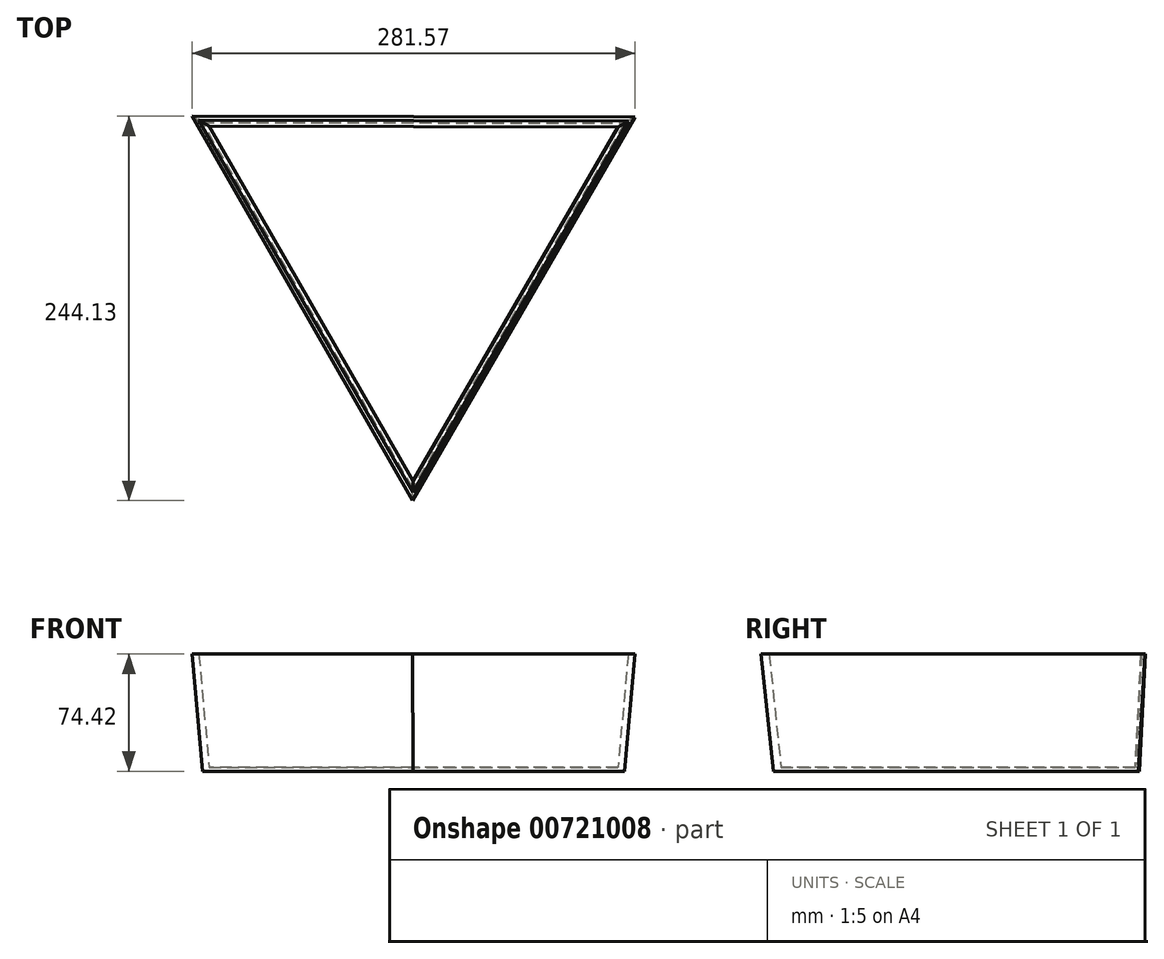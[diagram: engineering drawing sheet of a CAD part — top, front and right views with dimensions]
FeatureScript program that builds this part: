
annotation { "Feature Type Name" : "Feature", "Feature Type Description" : "" }
export const myFeature = defineFeature(function(context is Context, id is Id, definition is map)
    precondition{}
    {
        {
            var Q0;
            Q0=qCreatedBy(makeId("Top.planeOp"),FACE);
            var sketch = newSketch(context, id + "F0", { "sketchPlane" : qUnion([Q0])});
            skCircle(sketch, "E0.cCircle", {"center": v(0, -27.9) * mm, "radius": 77.38 * mm, "construction": true});
            skLineSegment(sketch, "E0.0", {"start": v(134.19, 49.2) * mm, "end": v(-0.32, -182.67) * mm});
            skLineSegment(sketch, "E0.1", {"start": v(-0.32, -182.67) * mm, "end": v(-133.87, 49.75) * mm});
            skLineSegment(sketch, "E0.2", {"start": v(-133.87, 49.75) * mm, "end": v(134.19, 49.2) * mm});
            skPoint(sketch, "E0.0.midPoint", {"position": v(66.94, -66.74) * mm});
            skSolve(sketch);
        }
        {
            var Q0;
            Q0=makeQuery(id+"F0.imprint","IMPRINT",FACE,{"disambiguationData":[TD([[makeQuery(id+"F0.imprint","IMPRINT",EDGE,{"derivedFrom":sQuery(id+"F0.wireOp",EDGE,"E0.0")}),-1.0]])]});
            extrude(context, id + "F1", {"entities" : qUnion([Q0]), "depth" : 74.42 * mm, "offsetDistance" : 25.4 * mm, "hasDraft" : true, "draftAngle" : 3 * degree});
        }
        {
            var Q0;
            Q0=makeQuery(id+"F1.opExtrude","CAP_FACE",FACE,{"disambiguationData":[OSD([sQuery(id+"F0.wireOp",EDGE,"E0.0"),sQuery(id+"F0.wireOp",EDGE,"E0.1"),sQuery(id+"F0.wireOp",EDGE,"E0.2")])],"isStart":false});
            shell(context, id + "F2", {"entities" : qUnion([Q0]), "thickness" : 2.54 * mm});
        }
    });
